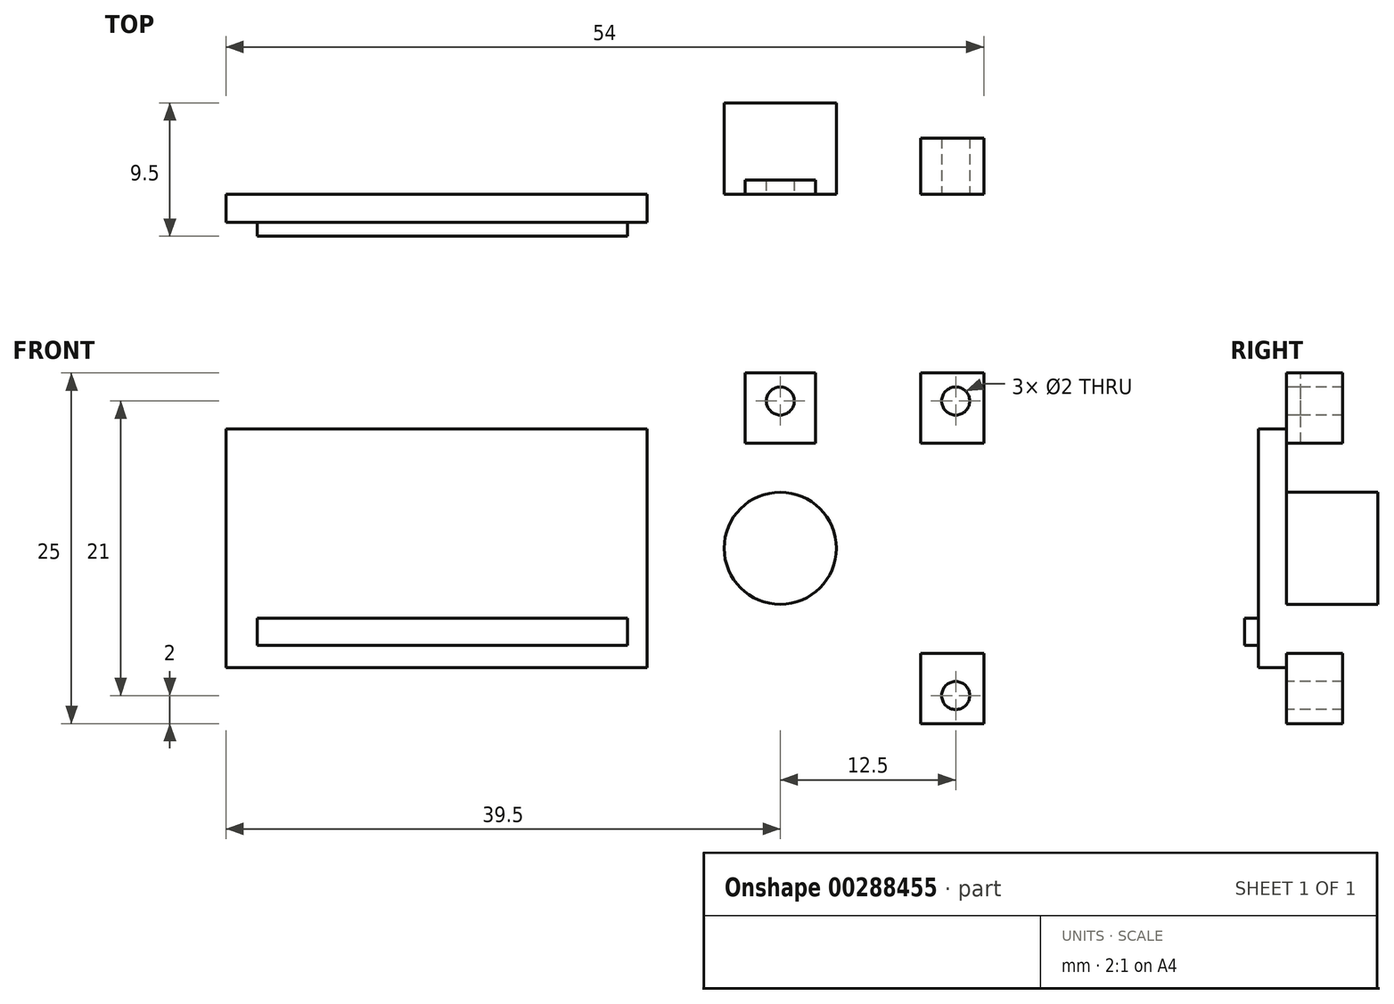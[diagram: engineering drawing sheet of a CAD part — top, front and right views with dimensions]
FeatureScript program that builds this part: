
annotation { "Feature Type Name" : "Feature", "Feature Type Description" : "" }
export const myFeature = defineFeature(function(context is Context, id is Id, definition is map)
    precondition{}
    {
        {
            var Q0;
            Q0=qCreatedBy(makeId("Front.planeOp"),FACE);
            var sketch = newSketch(context, id + "F0", { "sketchPlane" : qUnion([Q0])});
            skLineSegment(sketch, "E0.bottom", {"start": v(-12, 12.5) * mm, "end": v(12, 12.5) * mm});
            skLineSegment(sketch, "E0.top", {"start": v(-12, -12.5) * mm, "end": v(12, -12.5) * mm});
            skLineSegment(sketch, "E0.left", {"start": v(-12, 12.5) * mm, "end": v(-12, -12.5) * mm});
            skLineSegment(sketch, "E0.right", {"start": v(12, 12.5) * mm, "end": v(12, -12.5) * mm});
            skPoint(sketch, "E0.middle", {"position": v(0, 0) * mm});
            skCircle(sketch, "E1", {"center": v(-2.5, 0) * mm, "radius": 4 * mm});
            skLineSegment(sketch, "E2.bottom", {"start": v(12, 12.5) * mm, "end": v(7.5, 12.5) * mm});
            skLineSegment(sketch, "E2.top", {"start": v(12, 7.5) * mm, "end": v(7.5, 7.5) * mm});
            skLineSegment(sketch, "E2.left", {"start": v(12, 12.5) * mm, "end": v(12, 7.5) * mm});
            skLineSegment(sketch, "E2.right", {"start": v(7.5, 12.5) * mm, "end": v(7.5, 7.5) * mm});
            skLineSegment(sketch, "E3.bottom", {"start": v(12, -12.5) * mm, "end": v(7.5, -12.5) * mm});
            skLineSegment(sketch, "E3.top", {"start": v(12, -7.5) * mm, "end": v(7.5, -7.5) * mm});
            skLineSegment(sketch, "E3.left", {"start": v(12, -12.5) * mm, "end": v(12, -7.5) * mm});
            skLineSegment(sketch, "E3.right", {"start": v(7.5, -12.5) * mm, "end": v(7.5, -7.5) * mm});
            skLineSegment(sketch, "E4.bottom", {"start": v(-5, -12.5) * mm, "end": v(0, -12.5) * mm});
            skLineSegment(sketch, "E4.top", {"start": v(-5, -7.5) * mm, "end": v(0, -7.5) * mm});
            skLineSegment(sketch, "E4.left", {"start": v(-5, -12.5) * mm, "end": v(-5, -7.5) * mm});
            skLineSegment(sketch, "E4.right", {"start": v(0, -12.5) * mm, "end": v(0, -7.5) * mm});
            skLineSegment(sketch, "E5.bottom", {"start": v(0, 7.5) * mm, "end": v(-5, 7.5) * mm});
            skLineSegment(sketch, "E5.top", {"start": v(0, 12.5) * mm, "end": v(-5, 12.5) * mm});
            skLineSegment(sketch, "E5.left", {"start": v(0, 7.5) * mm, "end": v(0, 12.5) * mm});
            skLineSegment(sketch, "E5.right", {"start": v(-5, 7.5) * mm, "end": v(-5, 12.5) * mm});
            skCircle(sketch, "E6", {"center": v(10, 10.5) * mm, "radius": 1 * mm});
            skCircle(sketch, "E7", {"center": v(10, -10.5) * mm, "radius": 1 * mm});
            skCircle(sketch, "E8", {"center": v(-2.5, -10.5) * mm, "radius": 1 * mm});
            skCircle(sketch, "E9", {"center": v(-2.5, 10.5) * mm, "radius": 1 * mm});
            skLineSegment(sketch, "E10.bottom", {"start": v(-12, 8.5) * mm, "end": v(-42, 8.5) * mm});
            skLineSegment(sketch, "E10.top", {"start": v(-12, -8.5) * mm, "end": v(-42, -8.5) * mm});
            skLineSegment(sketch, "E10.left", {"start": v(-12, 8.5) * mm, "end": v(-12, -8.5) * mm});
            skLineSegment(sketch, "E10.right", {"start": v(-42, 8.5) * mm, "end": v(-42, -8.5) * mm});
            skLineSegment(sketch, "E11.bottom", {"start": v(-13.38, -4.98) * mm, "end": v(-39.78, -4.98) * mm});
            skLineSegment(sketch, "E11.top", {"start": v(-13.38, -6.93) * mm, "end": v(-39.78, -6.93) * mm});
            skLineSegment(sketch, "E11.left", {"start": v(-13.38, -4.98) * mm, "end": v(-13.38, -6.93) * mm});
            skLineSegment(sketch, "E11.right", {"start": v(-39.78, -4.98) * mm, "end": v(-39.78, -6.93) * mm});
            skSolve(sketch);
        }
        {
            var Q0;
            Q0=makeQuery(id+"F0.imprint","IMPRINT",FACE,{"disambiguationData":[TD([[makeQuery(id+"F0.imprint","IMPRINT",EDGE,{"derivedFrom":sQuery(id+"F0.wireOp",EDGE,"E0.right")}),-1.0]])]});
            extrude(context, id + "F1", {"entities" : qUnion([Q0]), "oppositeDirection" : true, "depth" : 4 * mm});
        }
        {
            var Q0;
            Q0=makeQuery(id+"F0.imprint","IMPRINT",FACE,{"disambiguationData":[TD([[makeQuery(id+"F0.imprint","IMPRINT",EDGE,{"derivedFrom":sQuery(id+"F0.wireOp",EDGE,"E10.bottom")}),1.0]])]});
            extrude(context, id + "F2", {"entities" : qUnion([Q0]), "depth" : 2 * mm});
        }
        {
            var Q0;
            Q0=makeQuery(id+"F0.imprint","IMPRINT",FACE,{"disambiguationData":[TD([[makeQuery(id+"F0.imprint","IMPRINT",EDGE,{"derivedFrom":sQuery(id+"F0.wireOp",EDGE,"E3.bottom")}),-1.0]])]});
            var Q1;
            Q1=makeQuery(id+"F0.imprint","IMPRINT",FACE,{"disambiguationData":[TD([[makeQuery(id+"F0.imprint","IMPRINT",EDGE,{"derivedFrom":sQuery(id+"F0.wireOp",EDGE,"E2.bottom")}),1.0]])]});
            var Q2;
            Q2=makeQuery(id+"F0.imprint","IMPRINT",FACE,{"disambiguationData":[TD([[makeQuery(id+"F0.imprint","IMPRINT",EDGE,{"derivedFrom":sQuery(id+"F0.wireOp",EDGE,"E5.bottom")}),-1.0]])]});
            var Q3;
            Q3=makeQuery(id+"F0.imprint","IMPRINT",FACE,{"disambiguationData":[TD([[makeQuery(id+"F0.imprint","IMPRINT",EDGE,{"derivedFrom":sQuery(id+"F0.wireOp",EDGE,"E4.bottom")}),1.0]])]});
            extrude(context, id + "F3", {"entities" : qUnion([Q0, Q1, Q2, Q3]), "operationType" : NewBodyOperationType.ADD, "oppositeDirection" : true, "depth" : 1 * mm});
        }
        {
            var Q0;
            Q0=makeQuery(id+"F0.imprint","IMPRINT",FACE,{"disambiguationData":[TD([[makeQuery(id+"F0.imprint","IMPRINT",EDGE,{"derivedFrom":sQuery(id+"F0.wireOp",EDGE,"E1")}),1.0]])]});
            extrude(context, id + "F4", {"entities" : qUnion([Q0]), "operationType" : NewBodyOperationType.ADD, "oppositeDirection" : true, "depth" : 6.5 * mm});
        }
        {
            var Q0;
            Q0=makeQuery(id+"F0.imprint","IMPRINT",FACE,{"disambiguationData":[TD([[makeQuery(id+"F0.imprint","IMPRINT",EDGE,{"derivedFrom":sQuery(id+"F0.wireOp",EDGE,"E11.bottom")}),1.0]])]});
            extrude(context, id + "F5", {"entities" : qUnion([Q0]), "operationType" : NewBodyOperationType.ADD, "depth" : 3 * mm});
        }
    });
